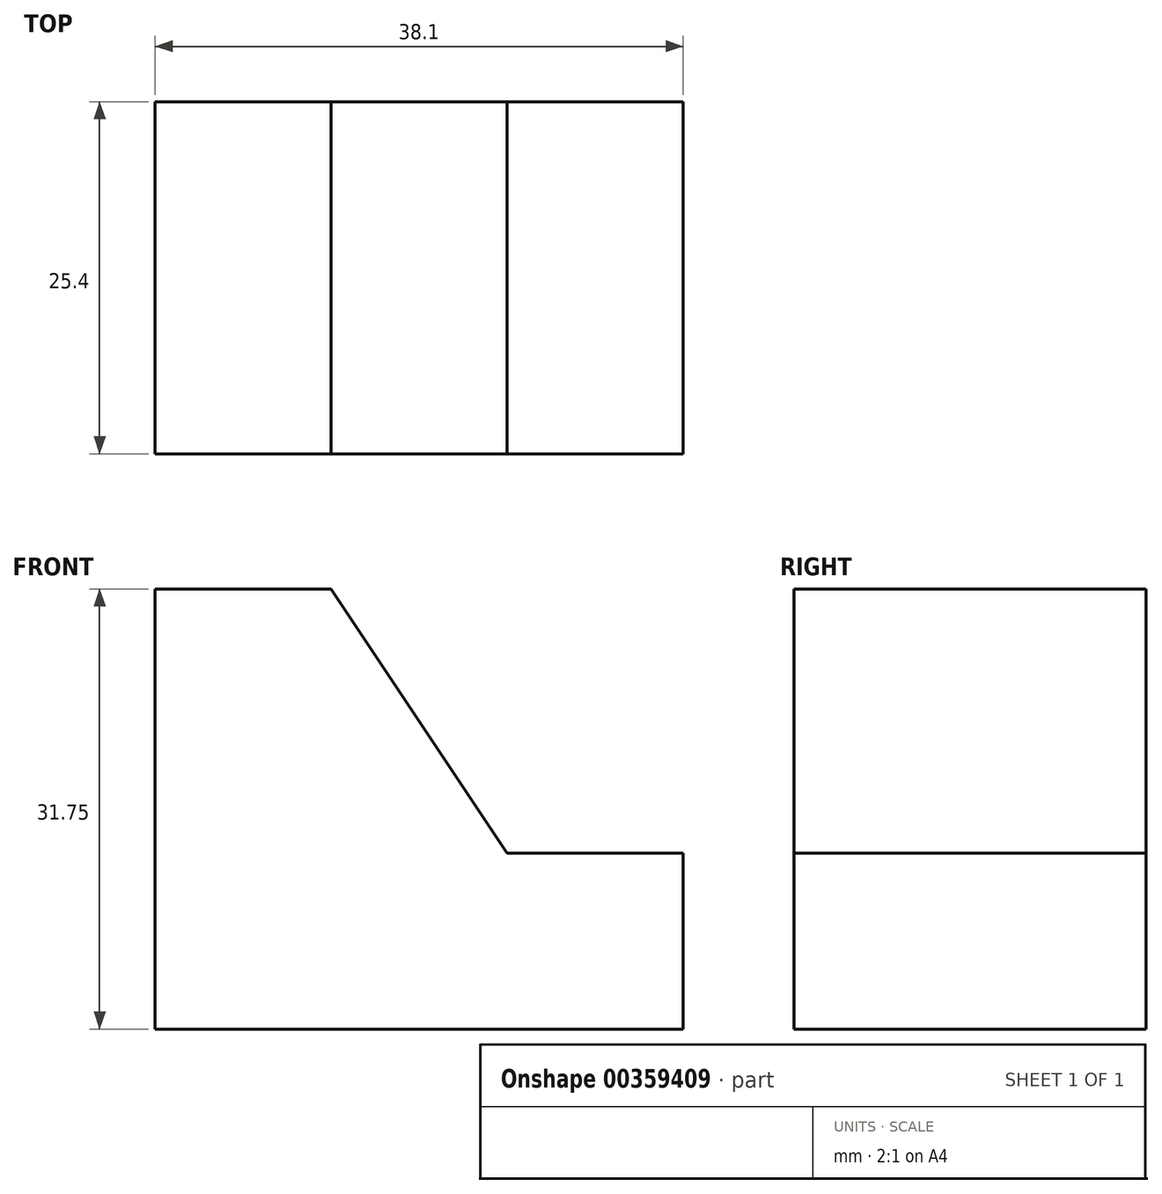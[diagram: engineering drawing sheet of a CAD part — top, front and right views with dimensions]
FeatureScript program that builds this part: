
annotation { "Feature Type Name" : "Feature", "Feature Type Description" : "" }
export const myFeature = defineFeature(function(context is Context, id is Id, definition is map)
    precondition{}
    {
        {
            var Q0;
            Q0=qCreatedBy(makeId("Front.planeOp"),FACE);
            var sketch = newSketch(context, id + "F0", { "sketchPlane" : qUnion([Q0])});
            skLineSegment(sketch, "E0", {"start": v(0, 0) * mm, "end": v(0, 31.75) * mm});
            skLineSegment(sketch, "E1", {"start": v(0, 31.75) * mm, "end": v(38.1, 31.75) * mm});
            skLineSegment(sketch, "E2", {"start": v(38.1, 31.75) * mm, "end": v(38.1, 0) * mm});
            skLineSegment(sketch, "E3", {"start": v(0, 0) * mm, "end": v(38.1, 0) * mm});
            skSolve(sketch);
        }
        {
            var Q0;
            Q0=makeQuery(id+"F0.imprint","IMPRINT",FACE,{"disambiguationData":[TD([[makeQuery(id+"F0.imprint","IMPRINT",EDGE,{"derivedFrom":sQuery(id+"F0.wireOp",EDGE,"E0")}),-1.0]])]});
            extrude(context, id + "F1", {"entities" : qUnion([Q0]), "depth" : 25.4 * mm});
        }
        {
            var Q0;
            Q0=makeQuery(id+"F1.opExtrude","CAP_FACE",FACE,{"disambiguationData":[OSD([sQuery(id+"F0.wireOp",EDGE,"E0"),sQuery(id+"F0.wireOp",EDGE,"E1"),sQuery(id+"F0.wireOp",EDGE,"E2"),sQuery(id+"F0.wireOp",EDGE,"E3")])],"isStart":false});
            var sketch = newSketch(context, id + "F2", { "sketchPlane" : qUnion([Q0])});
            skLineSegment(sketch, "E4", {"start": v(38.1, 12.7) * mm, "end": v(0, 12.7) * mm});
            skLineSegment(sketch, "E5", {"start": v(12.7, 31.75) * mm, "end": v(12.7, 0) * mm});
            skLineSegment(sketch, "E6", {"start": v(0, 31.75) * mm, "end": v(12.7, 31.75) * mm});
            skLineSegment(sketch, "E7", {"start": v(0, 0) * mm, "end": v(0, 12.7) * mm});
            skLineSegment(sketch, "E8", {"start": v(12.7, 31.75) * mm, "end": v(25.4, 12.7) * mm});
            skLineSegment(sketch, "E9", {"start": v(25.4, 12.7) * mm, "end": v(38.1, 12.7) * mm});
            skSolve(sketch);
        }
        {
            var Q0;
            {var subQ0=sQuery(id+"F2.wireOp",EDGE,"E8");Q0=makeQuery(id+"F2.imprint","IMPRINT",FACE,{"disambiguationData":[TD([[makeQuery(id+"F2.imprint","IMPRINT",EDGE,{"derivedFrom":subQ0}),1.0]])]});}
            extrude(context, id + "F3", {"entities" : qUnion([Q0]), "operationType" : NewBodyOperationType.REMOVE, "oppositeDirection" : true, "depth" : 25.4 * mm});
        }
    });
